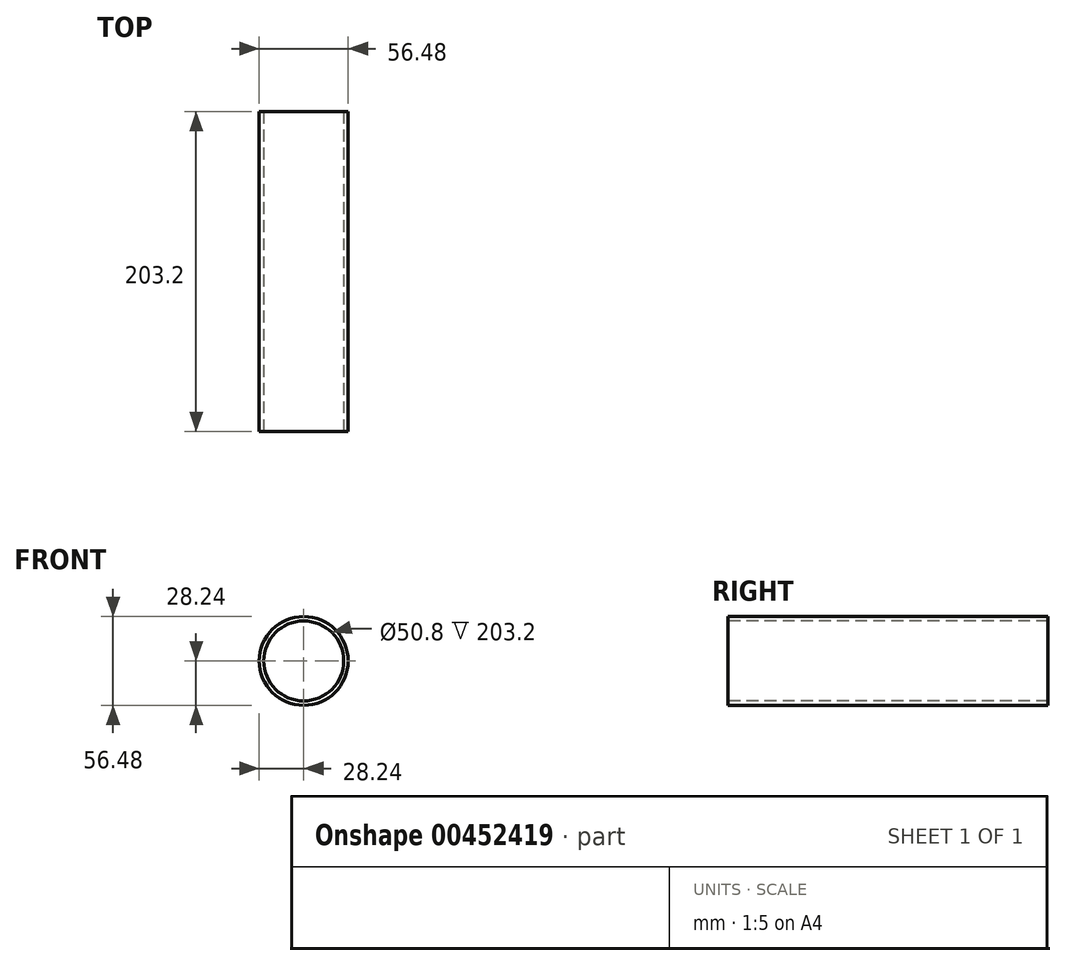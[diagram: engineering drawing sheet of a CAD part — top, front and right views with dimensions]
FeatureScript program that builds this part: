
annotation { "Feature Type Name" : "Feature", "Feature Type Description" : "" }
export const myFeature = defineFeature(function(context is Context, id is Id, definition is map)
    precondition{}
    {
        {
            var Q0;
            Q0=qCreatedBy(makeId("Front.planeOp"),FACE);
            var sketch = newSketch(context, id + "F0", { "sketchPlane" : qUnion([Q0])});
            skCircle(sketch, "E0", {"center": v(0, 0) * mm, "radius": 28.24 * mm});
            skSolve(sketch);
        }
        {
            var Q0;
            Q0=makeQuery(id+"F0.imprint","IMPRINT",FACE,{"disambiguationData":[TD([[makeQuery(id+"F0.imprint","IMPRINT",EDGE,{"derivedFrom":sQuery(id+"F0.wireOp",EDGE,"E0")}),1.0]])]});
            extrude(context, id + "F1", {"entities" : qUnion([Q0]), "depth" : 203.2 * mm});
        }
        {
            var Q0;
            Q0=makeQuery(id+"F1.opExtrude","CAP_FACE",FACE,{"disambiguationData":[OSD([sQuery(id+"F0.wireOp",EDGE,"E0")])],"isStart":false});
            var sketch = newSketch(context, id + "F2", { "sketchPlane" : qUnion([Q0])});
            skPoint(sketch, "E1", {"position": v(0, 0) * mm});
            skSolve(sketch);
        }
        {
            var Q0;
            Q0=sQuery(id+"F2.wireOp",VERTEX,"E1");
            var Q1;
            Q1=makeQuery(id+"F1.opExtrude","SWEPT_BODY",BODY,{"disambiguationData":[OSD([sQuery(id+"F0.wireOp",EDGE,"E0")])]});
            hole(context, id + "F3", {"style" : HoleStyle.SIMPLE, "endStyle" : HoleEndStyle.THROUGH, "holeDiameter" : 50.8 * mm, "isTappedThrough" : true, "tappedDepth" : 12.7 * mm, "tapClearance" : 3, "locations" : qUnion([Q0]), "scope" : qUnion([Q1])});
        }
    });
